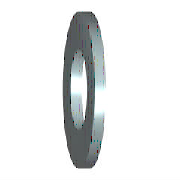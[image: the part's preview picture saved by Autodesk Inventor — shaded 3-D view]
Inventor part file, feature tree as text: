
AUTODESK INVENTOR PART (.ipt)
format: ipt  version: 2025.2 (Build 292293000, 293)  size: 104,960 bytes
history: native  units: mm (DEFAULTED — no unit token found)
features: extrude x1, other x1, plane x1
ambient origin geometry x7: Origin, YZ Plane, XY Plane, X Axis, Y Axis, Z Axis, Center Point
bodies: Solid1 (feature_tree)
feature tree (3):
  extrude  "Körper"  Depth=13.5mm
  other  "Work Axis1"
  plane  "Work Plane1"
